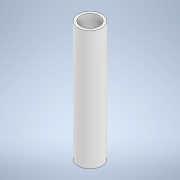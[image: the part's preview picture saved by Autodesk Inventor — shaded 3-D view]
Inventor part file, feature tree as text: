
AUTODESK INVENTOR PART (.ipt)
format: ipt  version: 2021 (Build 250183000, 183)  size: 98,816 bytes
history: native  units: mm
features: revolve x1, sketch x1
ambient origin geometry x8: Origin, YZ Plane, XZ Plane, XY Plane, X Axis, Y Axis, Z Axis, Center Point
bodies: Solid1 (feature_tree)
feature tree (2):
  revolve  "Revolution1"  [1 undecoded]
  sketch  "Sketch1"  dims[d1=20.0mm d2=15.5mm d3=200.0mm d4=90.0deg]
note: 1 required parameter value undecoded (feature->parameter linkage not recoverable at this tier; creation-order binding heuristic only, values carry confidence <= 0.55)
